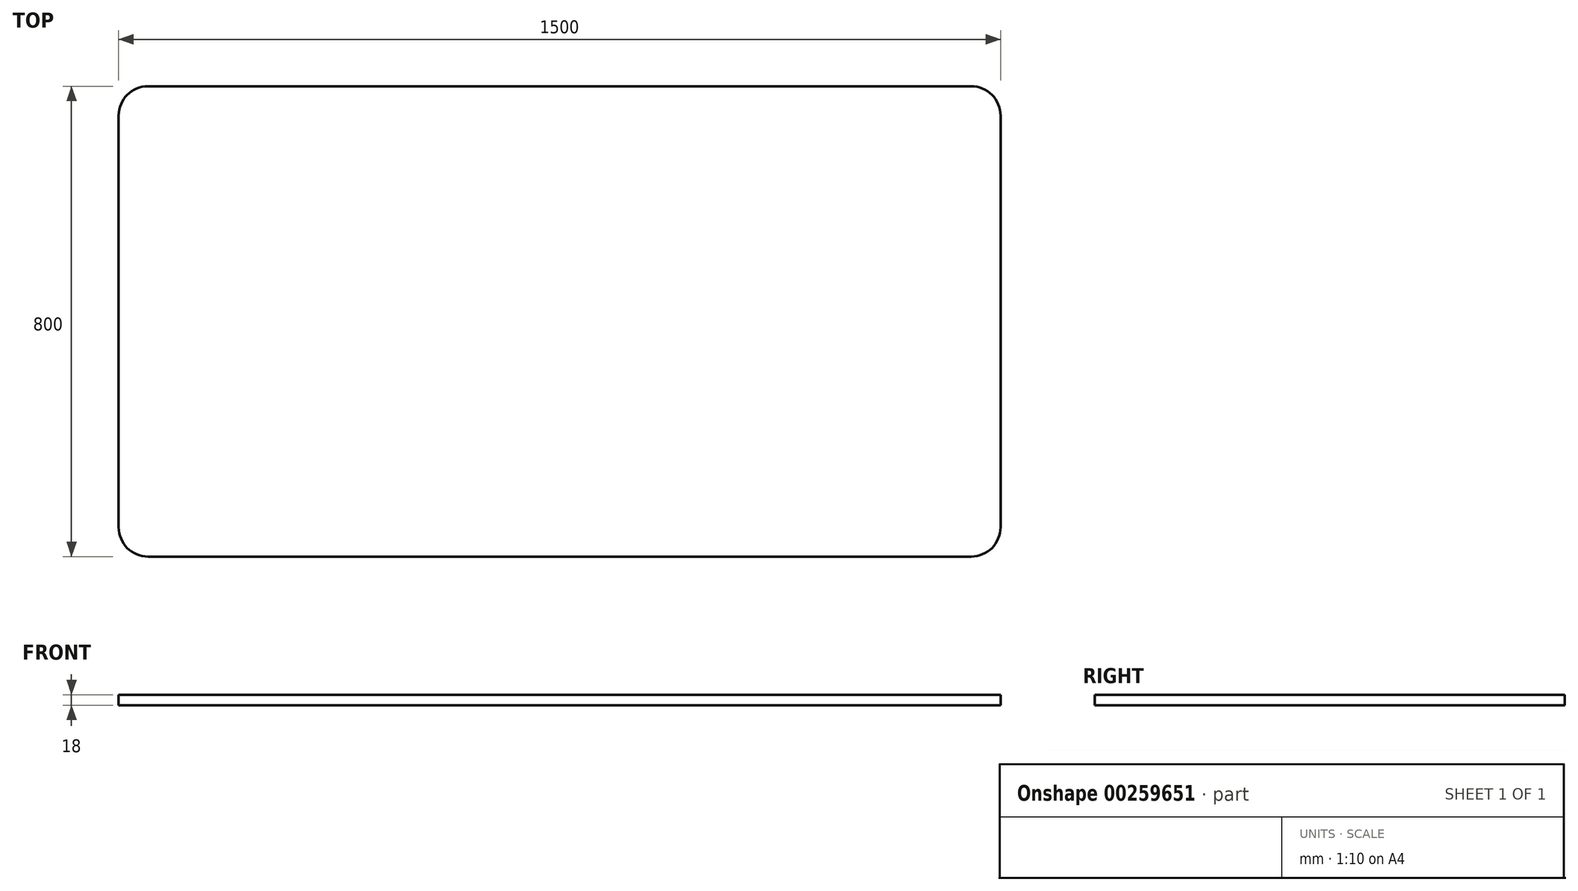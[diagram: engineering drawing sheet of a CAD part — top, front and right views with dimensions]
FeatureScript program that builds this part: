
annotation { "Feature Type Name" : "Feature", "Feature Type Description" : "" }
export const myFeature = defineFeature(function(context is Context, id is Id, definition is map)
    precondition{}
    {
        {
            var Q0;
            Q0=qCreatedBy(makeId("Top.planeOp"),FACE);
            var sketch = newSketch(context, id + "F0", { "sketchPlane" : qUnion([Q0])});
            skLineSegment(sketch, "E0.bottom", {"start": v(750, -400) * mm, "end": v(-750, -400) * mm});
            skLineSegment(sketch, "E0.top", {"start": v(750, 400) * mm, "end": v(-750, 400) * mm});
            skLineSegment(sketch, "E0.left", {"start": v(750, -400) * mm, "end": v(750, 400) * mm});
            skLineSegment(sketch, "E0.right", {"start": v(-750, -400) * mm, "end": v(-750, 400) * mm});
            skPoint(sketch, "E0.middle", {"position": v(0, 0) * mm});
            skSolve(sketch);
        }
        {
            var Q0;
            Q0 = qSketchRegion(id + "F0", true);
            extrude(context, id + "F1", {"entities" : qUnion([Q0]), "depth" : 18 * mm});
        }
        {
            var Q0;
            Q0=makeQuery(id+"F1.opExtrude","SWEPT_EDGE",EDGE,{"disambiguationData":[OSD([sQuery(id+"F0.wireOp",EDGE,"E0.bottom"),sQuery(id+"F0.wireOp",EDGE,"E0.right")])]});
            var Q1;
            Q1=makeQuery(id+"F1.opExtrude","SWEPT_EDGE",EDGE,{"disambiguationData":[OSD([sQuery(id+"F0.wireOp",EDGE,"E0.bottom"),sQuery(id+"F0.wireOp",EDGE,"E0.left")])]});
            var Q2;
            Q2=makeQuery(id+"F1.opExtrude","SWEPT_EDGE",EDGE,{"disambiguationData":[OSD([sQuery(id+"F0.wireOp",EDGE,"E0.top"),sQuery(id+"F0.wireOp",EDGE,"E0.left")])]});
            var Q3;
            Q3=makeQuery(id+"F1.opExtrude","SWEPT_EDGE",EDGE,{"disambiguationData":[OSD([sQuery(id+"F0.wireOp",EDGE,"E0.top"),sQuery(id+"F0.wireOp",EDGE,"E0.right")])]});
            fillet(context, id + "F2", {"entities" : qUnion([Q0, Q1, Q2, Q3]), "tangentPropagation" : true, "radius" : 50 * mm, "defaultsChanged" : false, "vertexSettings" : [], "allowEdgeOverflow" : false});
        }
    });
